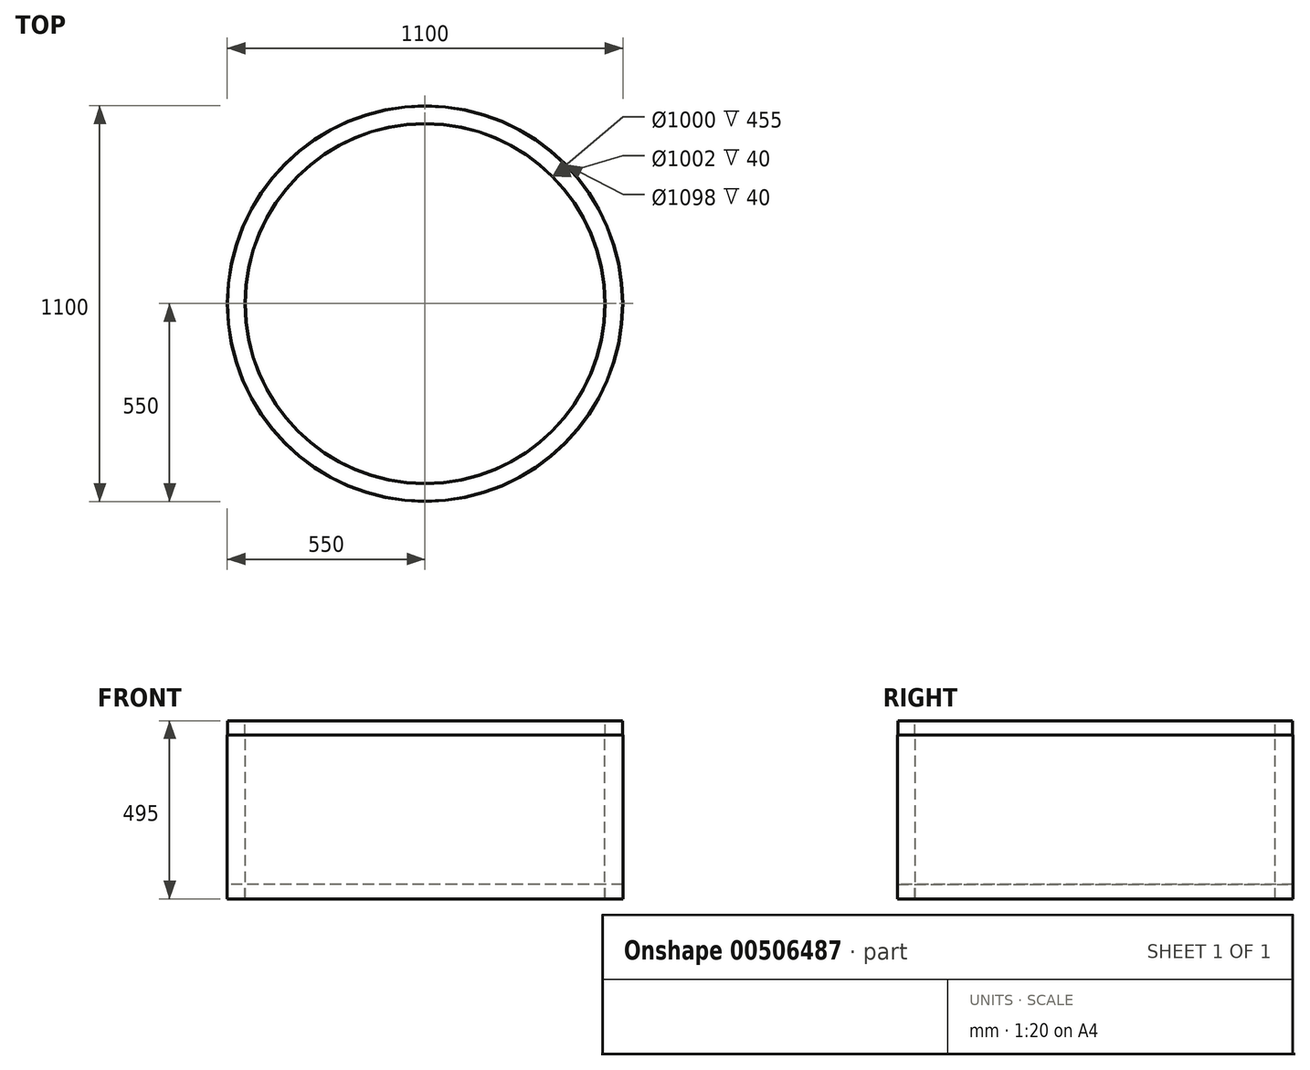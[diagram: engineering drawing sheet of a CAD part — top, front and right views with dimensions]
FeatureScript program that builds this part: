
annotation { "Feature Type Name" : "Feature", "Feature Type Description" : "" }
export const myFeature = defineFeature(function(context is Context, id is Id, definition is map)
    precondition{}
    {
        {
            var Q0;
            Q0=qCreatedBy(makeId("Front.planeOp"),FACE);
            var sketch = newSketch(context, id + "F0", { "sketchPlane" : qUnion([Q0])});
            skLineSegment(sketch, "E0", {"start": v(0, 74.87) * mm, "end": v(0, -73.71) * mm, "construction": true});
            skLineSegment(sketch, "E1", {"start": v(0, 374.84) * mm, "end": v(0, -528.94) * mm, "construction": true});
            skLineSegment(sketch, "E2", {"start": v(-500, -489.75) * mm, "end": v(-500, -34.75) * mm});
            skLineSegment(sketch, "E3", {"start": v(-500, -34.75) * mm, "end": v(-501, -34.75) * mm});
            skLineSegment(sketch, "E4", {"start": v(-501, -34.75) * mm, "end": v(-501, 5.25) * mm});
            skLineSegment(sketch, "E5", {"start": v(-501, 5.25) * mm, "end": v(-549, 5.25) * mm});
            skLineSegment(sketch, "E6", {"start": v(-549, 5.25) * mm, "end": v(-549, -34.75) * mm});
            skLineSegment(sketch, "E7", {"start": v(-549, -34.75) * mm, "end": v(-550, -34.75) * mm});
            skLineSegment(sketch, "E8", {"start": v(-550, -34.75) * mm, "end": v(-550, -489.75) * mm});
            skLineSegment(sketch, "E9", {"start": v(-550, -489.75) * mm, "end": v(-549, -489.75) * mm});
            skLineSegment(sketch, "E10", {"start": v(-549, -489.75) * mm, "end": v(-549, -449.75) * mm});
            skLineSegment(sketch, "E11", {"start": v(-549, -449.75) * mm, "end": v(-501, -449.75) * mm});
            skLineSegment(sketch, "E12", {"start": v(-501, -449.75) * mm, "end": v(-501, -489.75) * mm});
            skLineSegment(sketch, "E13", {"start": v(-501, -489.75) * mm, "end": v(-500, -489.75) * mm});
            skSolve(sketch);
        }
        {
            var Q0;
            Q0=qSketchRegion(id+"F0",true);
            var Q1;
            Q1=sQuery(id+"F0.wireOp",EDGE,"E1");
            revolve(context, id + "F1", {"entities" : qUnion([Q0]), "axis" : qUnion([Q1]), "revolveType" : RevolveType.FULL});
        }
    });
